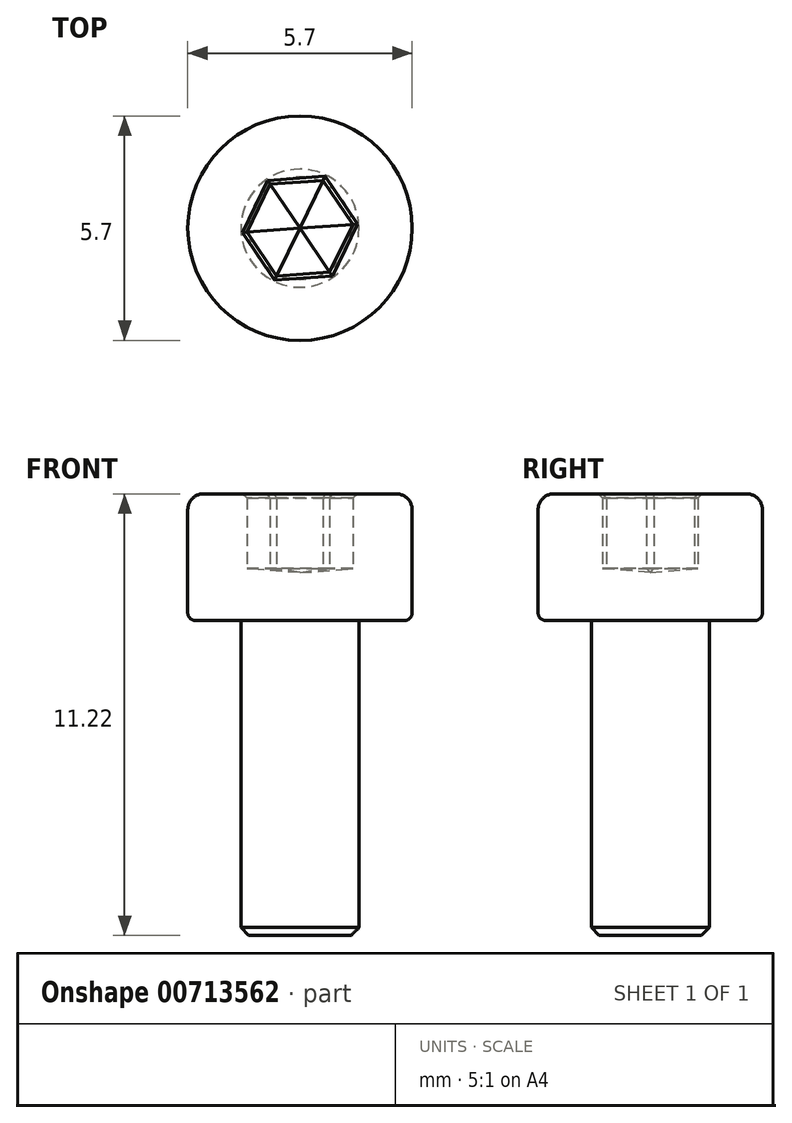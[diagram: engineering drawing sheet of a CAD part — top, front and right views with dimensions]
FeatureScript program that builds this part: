
annotation { "Feature Type Name" : "Feature", "Feature Type Description" : "" }
export const myFeature = defineFeature(function(context is Context, id is Id, definition is map)
    precondition{}
    {
        {
            var Q0;
            Q0=qCreatedBy(makeId("Top.planeOp"),FACE);
            var sketch = newSketch(context, id + "F0", { "sketchPlane" : qUnion([Q0])});
            skCircle(sketch, "E0", {"center": v(0, 0) * mm, "radius": 2.85 * mm});
            skCircle(sketch, "E1", {"center": v(0, 0) * mm, "radius": 1.5 * mm});
            skCircle(sketch, "E2.cCircle", {"center": v(0, 0) * mm, "radius": 1.35 * mm, "construction": true});
            skLineSegment(sketch, "E2.0", {"start": v(-0.76, 1.12) * mm, "end": v(0.59, 1.21) * mm});
            skLineSegment(sketch, "E2.1", {"start": v(0.59, 1.21) * mm, "end": v(1.35, 0.1) * mm});
            skLineSegment(sketch, "E2.2", {"start": v(1.35, 0.1) * mm, "end": v(0.76, -1.12) * mm});
            skLineSegment(sketch, "E2.3", {"start": v(0.76, -1.12) * mm, "end": v(-0.59, -1.21) * mm});
            skLineSegment(sketch, "E2.4", {"start": v(-0.59, -1.21) * mm, "end": v(-1.35, -0.1) * mm});
            skLineSegment(sketch, "E2.5", {"start": v(-1.35, -0.1) * mm, "end": v(-0.76, 1.12) * mm});
            skSolve(sketch);
        }
        {
            var Q0;
            Q0=qSketchRegion(id+"F0",true);
            var Q1;
            Q1=makeQuery(id+"F0.imprint","IMPRINT",FACE,{"disambiguationData":[TD([[makeQuery(id+"F0.imprint","IMPRINT",EDGE,{"derivedFrom":sQuery(id+"F0.wireOp",EDGE,"E1")}),1.0]])]});
            var Q2;
            Q2=makeQuery(id+"F0.imprint","IMPRINT",FACE,{"disambiguationData":[TD([[makeQuery(id+"F0.imprint","IMPRINT",EDGE,{"derivedFrom":sQuery(id+"F0.wireOp",EDGE,"E2.0")}),-1.0]])]});
            extrude(context, id + "F1", {"entities" : qUnion([Q0, Q1, Q2]), "depth" : 3.22 * mm});
        }
        {
            var Q0;
            Q0=makeQuery(id+"F0.imprint","IMPRINT",FACE,{"disambiguationData":[TD([[makeQuery(id+"F0.imprint","IMPRINT",EDGE,{"derivedFrom":sQuery(id+"F0.wireOp",EDGE,"E1")}),1.0]])]});
            var Q1;
            Q1=makeQuery(id+"F0.imprint","IMPRINT",FACE,{"disambiguationData":[TD([[makeQuery(id+"F0.imprint","IMPRINT",EDGE,{"derivedFrom":sQuery(id+"F0.wireOp",EDGE,"E2.0")}),-1.0]])]});
            extrude(context, id + "F2", {"entities" : qUnion([Q0, Q1]), "operationType" : NewBodyOperationType.ADD, "oppositeDirection" : true, "depth" : 8 * mm});
        }
        {
            var Q0;
            Q0=makeQuery(id+"F1.opExtrude","CAP_EDGE",EDGE,{"disambiguationData":[OSD([sQuery(id+"F0.wireOp",EDGE,"E0")])],"isStart":false});
            fillet(context, id + "F3", {"entities" : qUnion([Q0]), "radius" : 0.4 * mm, "tangentPropagation" : true, "allowEdgeOverflow" : false});
        }
        {
            var Q0;
            Q0=makeQuery(id+"F1.opExtrude","CAP_EDGE",EDGE,{"disambiguationData":[OSD([sQuery(id+"F0.wireOp",EDGE,"E0")])],"isStart":true});
            fillet(context, id + "F4", {"entities" : qUnion([Q0]), "radius" : 0.2 * mm, "tangentPropagation" : true, "allowEdgeOverflow" : false});
        }
        {
            var Q0;
            Q0=makeQuery(id+"F2.opExtrude","CAP_EDGE",EDGE,{"disambiguationData":[OSD([sQuery(id+"F0.wireOp",EDGE,"E1")])],"isStart":false});
            chamfer(context, id + "F5", {"entities" : qUnion([Q0]), "width" : 0.2 * mm, "tangentPropagation" : true});
        }
        {
            var Q0;
            Q0=makeQuery(id+"F0.imprint","IMPRINT",FACE,{"disambiguationData":[TD([[makeQuery(id+"F0.imprint","IMPRINT",EDGE,{"derivedFrom":sQuery(id+"F0.wireOp",EDGE,"E2.0")}),-1.0]])]});
            extrude(context, id + "F6", {"entities" : qUnion([Q0]), "operationType" : NewBodyOperationType.REMOVE, "depth" : 25 * mm, "hasSecondDirection" : true, "secondDirectionOppositeDirection" : false, "secondDirectionDepth" : (3.22 - 1.9) * mm});
        }
        {
            var Q0;
            Q0=makeQuery(id+"F6.boolean.opBoolean","INTERSECT",EDGE,{"derivedFrom":[makeQuery(id+"F1.opExtrude","CAP_FACE",FACE,{"disambiguationData":[OSD([sQuery(id+"F0.wireOp",EDGE,"E0")])],"isStart":false}),makeQuery(id+"F6.opExtrude","SWEPT_FACE",FACE,{"disambiguationData":[OSD([sQuery(id+"F0.wireOp",EDGE,"E2.5")])]})]});
            var Q1;
            Q1=makeQuery(id+"F6.boolean.opBoolean","INTERSECT",EDGE,{"derivedFrom":[makeQuery(id+"F1.opExtrude","CAP_FACE",FACE,{"disambiguationData":[OSD([sQuery(id+"F0.wireOp",EDGE,"E0")])],"isStart":false}),makeQuery(id+"F6.opExtrude","SWEPT_FACE",FACE,{"disambiguationData":[OSD([sQuery(id+"F0.wireOp",EDGE,"E2.0")])]})]});
            var Q2;
            Q2=makeQuery(id+"F6.boolean.opBoolean","INTERSECT",EDGE,{"derivedFrom":[makeQuery(id+"F1.opExtrude","CAP_FACE",FACE,{"disambiguationData":[OSD([sQuery(id+"F0.wireOp",EDGE,"E0")])],"isStart":false}),makeQuery(id+"F6.opExtrude","SWEPT_FACE",FACE,{"disambiguationData":[OSD([sQuery(id+"F0.wireOp",EDGE,"E2.1")])]})]});
            var Q3;
            Q3=makeQuery(id+"F6.boolean.opBoolean","INTERSECT",EDGE,{"derivedFrom":[makeQuery(id+"F1.opExtrude","CAP_FACE",FACE,{"disambiguationData":[OSD([sQuery(id+"F0.wireOp",EDGE,"E0")])],"isStart":false}),makeQuery(id+"F6.opExtrude","SWEPT_FACE",FACE,{"disambiguationData":[OSD([sQuery(id+"F0.wireOp",EDGE,"E2.2")])]})]});
            var Q4;
            Q4=makeQuery(id+"F6.boolean.opBoolean","INTERSECT",EDGE,{"derivedFrom":[makeQuery(id+"F1.opExtrude","CAP_FACE",FACE,{"disambiguationData":[OSD([sQuery(id+"F0.wireOp",EDGE,"E0")])],"isStart":false}),makeQuery(id+"F6.opExtrude","SWEPT_FACE",FACE,{"disambiguationData":[OSD([sQuery(id+"F0.wireOp",EDGE,"E2.3")])]})]});
            var Q5;
            Q5=makeQuery(id+"F6.boolean.opBoolean","INTERSECT",EDGE,{"derivedFrom":[makeQuery(id+"F1.opExtrude","CAP_FACE",FACE,{"disambiguationData":[OSD([sQuery(id+"F0.wireOp",EDGE,"E0")])],"isStart":false}),makeQuery(id+"F6.opExtrude","SWEPT_FACE",FACE,{"disambiguationData":[OSD([sQuery(id+"F0.wireOp",EDGE,"E2.4")])]})]});
            chamfer(context, id + "F7", {"entities" : qUnion([Q0, Q1, Q2, Q3, Q4, Q5]), "width" : 0.1 * mm, "tangentPropagation" : true});
        }
        {
            var Q0;
            Q0=makeQuery(id+"F6.boolean.opBoolean","COPY",FACE,{"derivedFrom":makeQuery(id+"F6.opExtrude","CAP_FACE",FACE,{"disambiguationData":[OSD([sQuery(id+"F0.wireOp",EDGE,"E2.0"),sQuery(id+"F0.wireOp",EDGE,"E2.1"),sQuery(id+"F0.wireOp",EDGE,"E2.2"),sQuery(id+"F0.wireOp",EDGE,"E2.3"),sQuery(id+"F0.wireOp",EDGE,"E2.4"),sQuery(id+"F0.wireOp",EDGE,"E2.5")])],"isStart":true})});
            extrude(context, id + "F8", {"entities" : qUnion([Q0]), "operationType" : NewBodyOperationType.REMOVE, "oppositeDirection" : true, "depth" : 0.2 * mm, "hasDraft" : true, "draftAngle" : 85 * degree, "draftPullDirection" : true});
        }
    });
